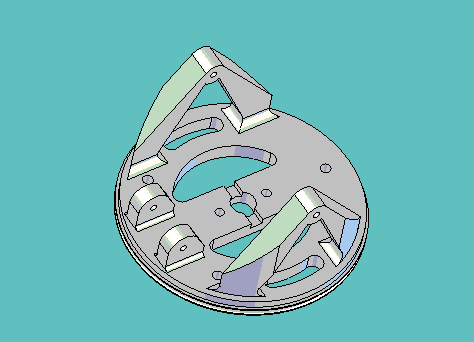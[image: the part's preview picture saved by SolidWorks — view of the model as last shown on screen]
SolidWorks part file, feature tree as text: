
SOLIDWORKS PART (.sldprt)
format: sldprt  version: not decoded by parser v0  size: 1,469,440 bytes
history: native  units: mm
features: sketch x17, cut_extrude x11, plane x7, extrude x5, fillet x3, material x1, revolve x1 (+11 scaffold rows collapsed)
feature tree (56):
  scaffold x11  (default folders/planes/origin — collapsed)
  material  "Material <not specified>"
  sketch  "Sketch1"  dims[c1.D1=50.8mm c1.D7=3.175mm c2.D1=88.9mm c2.D2=~93.32036mm c3.D2=45.0deg c3.D3=~94.913632mm c4.D3=45.0deg c4.D4=6.35mm c4.D5=6.35mm c4.D6=31.75mm]
  extrude  "Extrude1"  Depth=6.35mm
  sketch  "Sketch3"  dims[c1.D1=3.4544mm c1.D2=3.4544mm c1.D3=9.525mm c2.D2=3.4544mm c2.D4=3.4544mm c2.D1=~19.84375mm c2.D5=~22.869813mm c3.D5=30.0deg]
  cut_extrude  "Cut-Extrude2"  [1 undecoded]
  sketch  "Sketch5"  dims[c1.D3=19.05mm c1.D4=25.4mm c1.D1=20.6375mm c1.D2=20.6375mm c1.D5=~49.79749mm c2.D5=30.0deg c2.D6=11.1125mm c2.D1=17.145mm c2.D2=17.145mm c3.D1=~82.457251mm c4.D1=90.0deg c4.D2=9.525mm c4.D3=9.525mm]
  cut_extrude  "Cut-Extrude4"  [1 undecoded]
  sketch  "Sketch25"  dims[D1=4.7625mm]
  cut_extrude  "Cut-Extrude18"  [1 undecoded]
  fillet  "Fillet2"  Radius=3.175mm
  sketch  "Sketch6"  dims[D1=9.525mm]
  extrude  "Axis2"  [1 undecoded]
  plane  "Plane1"
  plane  "Plane2"
  plane  "Plane3"  Offset=50.8mm
  sketch  "Sketch11"  dims[c1.D1=40.3225mm c1.D2=40.3225mm c2.D1=22.86mm c2.D2=24.384mm c2.D3=30.1625mm c2.D4=30.1625mm]
  extrude  "Extrude6"  Depth=44.45mm
  sketch  "Sketch7"  dims[D1=2.7051mm D2=4.7625mm]
  cut_extrude  "Cut-Extrude7"  [1 undecoded]
  sketch  "Sketch12"  dims[D1=6.35mm D2=6.35mm D3=6.35mm]
  cut_extrude  "Cut-Extrude9"  [1 undecoded]
  sketch  "Sketch15"  dims[c1.D4=3.175mm c1.D1=9.525mm c1.D2=9.525mm c1.D3=9.525mm c2.D1=9.525mm c2.D2=9.525mm c2.D5=25.4mm c2.D6=25.4mm]
  cut_extrude  "Cut-Extrude12"  [1 undecoded]
  fillet  "Fillet3"  Radius=3.175mm
  plane  "Plane4"  Offset=7.14375mm
  plane  "Plane5"  Offset=7.14375mm
  sketch  "Sketch17"  dims[c1.D4=2.7051mm c1.D1=28.575mm c1.D2=9.525mm c1.D3=6.35mm c2.D1=34.925mm c2.D5=~9.745748mm c2.D3=9.525mm c3.D5=6.35mm c3.D6=6.35mm c3.D2=~11.90625mm c4.D5=~8.73125mm c4.D7=4.7625mm]
  extrude  "Extrude8"  Depth=5.969mm
  sketch  "Sketch18"  dims[D1=0.0mm]
  extrude  "Extrude9"  Depth=5.969mm
  fillet  "Fillet5"  Radius=1.5875mm
  plane  "Plane6"  Offset=39.6875mm
  plane  "Plane7"  Offset=39.6875mm
  sketch  "Sketch19"  dims[D1=12.7mm]
  cut_extrude  "Cut-Extrude14"  [1 undecoded]
  sketch  "Sketch20"
  cut_extrude  "Cut-Extrude15"  [1 undecoded]
  sketch  "Sketch21"  dims[D1=~2.38125mm]
  cut_extrude  "Cut-Extrude16"  [1 undecoded]
  sketch  "Sketch26"  dims[c1.D2=~2.38125mm c1.D1=3.175mm c1.D3=0.508mm c1.D4=1.5875mm c1.D5=46.101mm c1.D6=44.45mm c2.D1=3.175mm]
  revolve  "Revolve1"  Angle=360deg
  sketch  "Sketch24"  dims[c1.D1=~3.96875mm c1.D2=~3.96875mm c1.D3=~3.96875mm c1.D5=69.85mm c1.D4=~57.085134mm c2.D4=30.0deg c2.D6=~57.085134mm c3.D6=137.0deg c3.D7=~57.085134mm c4.D7=137.0deg]
  cut_extrude  "Cut-Extrude17"  [1 undecoded]
  sketch  "Sketch27"  dims[c1.D1=82.55mm c1.D4=6.35mm c1.D5=60.325mm c1.D2=~49.526136mm c2.D2=30.0deg c3.D2=~53.156372mm c4.D2=30.0deg c4.D3=35.56mm c4.D6=~50.104381mm c5.D6=15.0deg c5.D7=~51.861275mm c6.D7=15.0deg]
  cut_extrude  "Cut-Extrude19"  [1 undecoded]
decode coverage: 24 of 37 modeling features carry decoded parameters
note: ~ marks probable driven/reference dimensions
note: 12 parameter values undecoded
summary: no parameter record found for 12 features
note: suppression state not decoded; provenance and decode notes live in map.json
